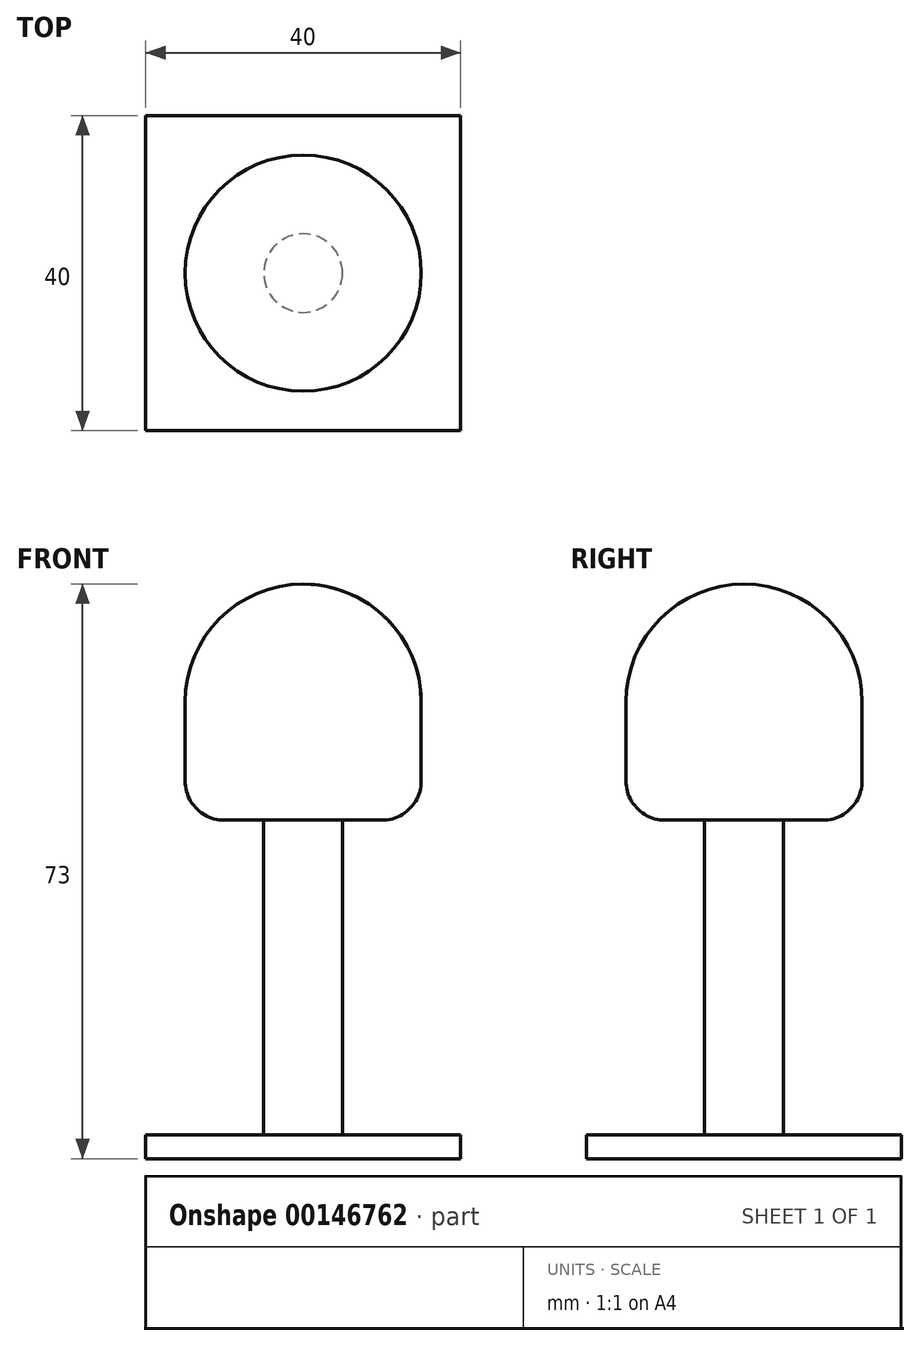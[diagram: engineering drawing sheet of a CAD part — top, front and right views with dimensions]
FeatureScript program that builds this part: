
annotation { "Feature Type Name" : "Feature", "Feature Type Description" : "" }
export const myFeature = defineFeature(function(context is Context, id is Id, definition is map)
    precondition{}
    {
        {
            var Q0;
            Q0=qCreatedBy(makeId("Top.planeOp"),FACE);
            var sketch = newSketch(context, id + "F0", { "sketchPlane" : qUnion([Q0])});
            skLineSegment(sketch, "E0.bottom", {"start": v(-20, 20) * mm, "end": v(20, 20) * mm});
            skLineSegment(sketch, "E0.top", {"start": v(-20, -20) * mm, "end": v(20, -20) * mm});
            skLineSegment(sketch, "E0.left", {"start": v(-20, 20) * mm, "end": v(-20, -20) * mm});
            skLineSegment(sketch, "E0.right", {"start": v(20, 20) * mm, "end": v(20, -20) * mm});
            skPoint(sketch, "E0.middle", {"position": v(0, 0) * mm});
            skSolve(sketch);
        }
        {
            var Q0;
            Q0 = qSketchRegion(id + "F0", true);
            extrude(context, id + "F1", {"entities" : qUnion([Q0]), "depth" : 3 * mm});
        }
        {
            var Q0;
            Q0=makeQuery(id+"F1.opExtrude","CAP_FACE",FACE,{"disambiguationData":[OSD([sQuery(id+"F0.wireOp",EDGE,"E0.bottom"),sQuery(id+"F0.wireOp",EDGE,"E0.top"),sQuery(id+"F0.wireOp",EDGE,"E0.left"),sQuery(id+"F0.wireOp",EDGE,"E0.right")])],"isStart":false});
            var sketch = newSketch(context, id + "F2", { "sketchPlane" : qUnion([Q0])});
            skCircle(sketch, "E1", {"center": v(0, 0) * mm, "radius": 5 * mm});
            skSolve(sketch);
        }
        {
            var Q0;
            Q0 = qSketchRegion(id + "F2", true);
            extrude(context, id + "F3", {"entities" : qUnion([Q0]), "operationType" : NewBodyOperationType.ADD, "depth" : 40 * mm});
        }
        {
            var Q0;
            Q0=makeQuery(id+"F3.opExtrude","CAP_FACE",FACE,{"disambiguationData":[OSD([sQuery(id+"F2.wireOp",EDGE,"E1")])],"isStart":false});
            var sketch = newSketch(context, id + "F4", { "sketchPlane" : qUnion([Q0])});
            skCircle(sketch, "E2", {"center": v(0, 0) * mm, "radius": 15 * mm});
            skSolve(sketch);
        }
        {
            var Q0;
            Q0 = qSketchRegion(id + "F4", true);
            extrude(context, id + "F5", {"entities" : qUnion([Q0]), "operationType" : NewBodyOperationType.ADD, "depth" : 30 * mm});
        }
        {
            var Q0;
            Q0=makeQuery(id+"F5.opExtrude","CAP_EDGE",EDGE,{"disambiguationData":[OSD([sQuery(id+"F4.wireOp",EDGE,"E2")])],"isStart":false});
            fillet(context, id + "F6", {"entities" : qUnion([Q0]), "radius" : 15 * mm, "tangentPropagation" : true, "allowEdgeOverflow" : false});
        }
        {
            var Q0;
            Q0=makeQuery(id+"F5.opExtrude","CAP_EDGE",EDGE,{"disambiguationData":[OSD([sQuery(id+"F4.wireOp",EDGE,"E2")])],"isStart":true});
            fillet(context, id + "F7", {"entities" : qUnion([Q0]), "radius" : 5 * mm, "tangentPropagation" : true, "allowEdgeOverflow" : false});
        }
    });
